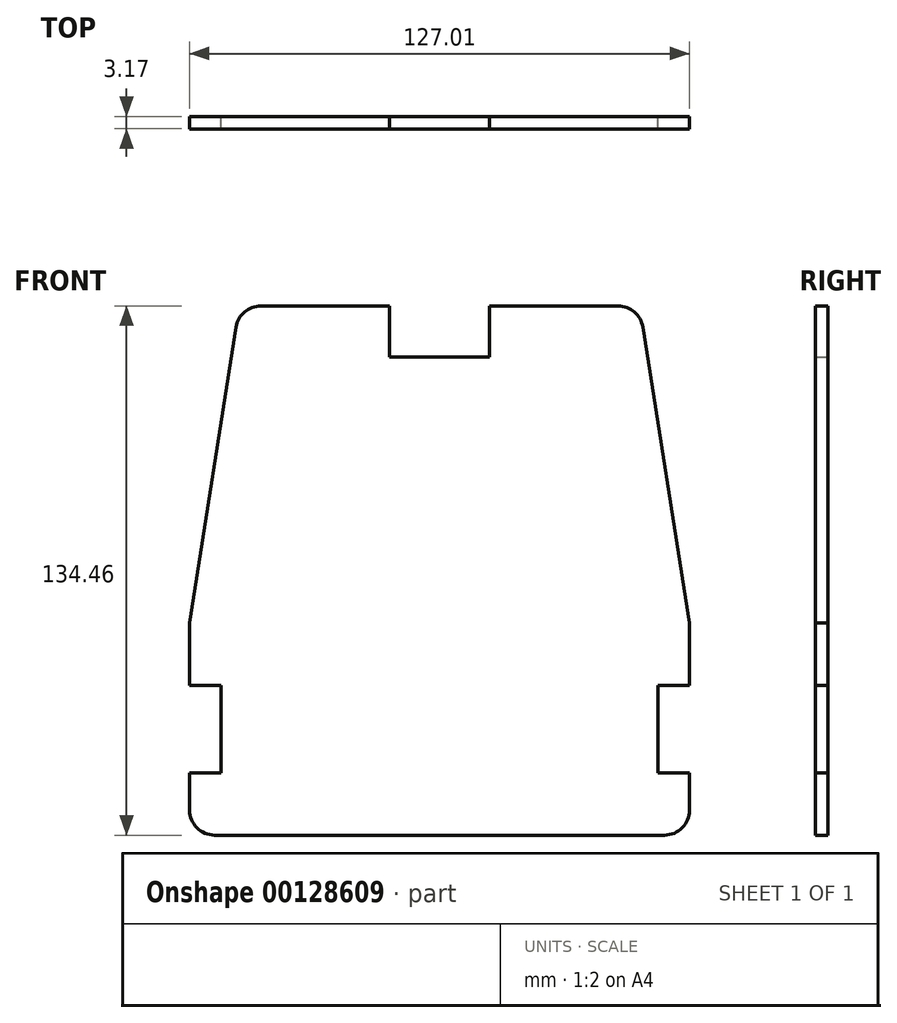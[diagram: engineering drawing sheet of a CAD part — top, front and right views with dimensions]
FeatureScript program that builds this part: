
annotation { "Feature Type Name" : "Feature", "Feature Type Description" : "" }
export const myFeature = defineFeature(function(context is Context, id is Id, definition is map)
    precondition{}
    {
        {
            var Q0;
            Q0=qCreatedBy(makeId("Front.planeOp"),FACE);
            var sketch = newSketch(context, id + "F0", { "sketchPlane" : qUnion([Q0])});
            skLineSegment(sketch, "E0.bottom", {"start": v(-50.8, -3.65) * mm, "end": v(76.2, -3.65) * mm});
            skLineSegment(sketch, "E0.top", {"start": v(-44.44, -57.63) * mm, "end": v(69.86, -57.63) * mm});
            skLineSegment(sketch, "E1", {"start": v(-38.95, 71.47) * mm, "end": v(-50.8, -3.65) * mm});
            skLineSegment(sketch, "E2", {"start": v(64.35, 71.47) * mm, "end": v(76.2, -3.65) * mm});
            skLineSegment(sketch, "E3", {"start": v(-32.67, 76.83) * mm, "end": v(0, 76.83) * mm});
            skLineSegment(sketch, "E4", {"start": v(58.07, 76.83) * mm, "end": v(25.4, 76.83) * mm});
            skLineSegment(sketch, "E5", {"start": v(-50.79, -41.75) * mm, "end": v(-42.85, -41.75) * mm});
            skLineSegment(sketch, "E6", {"start": v(-50.8, -19.53) * mm, "end": v(-42.85, -19.53) * mm});
            skLineSegment(sketch, "E7", {"start": v(-42.85, -19.53) * mm, "end": v(-42.85, -41.75) * mm});
            skLineSegment(sketch, "E8", {"start": v(-50.8, -19.53) * mm, "end": v(-50.8, -3.65) * mm});
            skLineSegment(sketch, "E9", {"start": v(-50.79, -41.75) * mm, "end": v(-50.79, -51.28) * mm});
            skLineSegment(sketch, "E10", {"start": v(76.2, -3.65) * mm, "end": v(76.2, -19.53) * mm});
            skLineSegment(sketch, "E11", {"start": v(76.21, -51.28) * mm, "end": v(76.21, -41.75) * mm});
            skLineSegment(sketch, "E12", {"start": v(76.2, -19.53) * mm, "end": v(68.25, -19.53) * mm});
            skLineSegment(sketch, "E13", {"start": v(68.25, -19.53) * mm, "end": v(68.25, -41.75) * mm});
            skLineSegment(sketch, "E14", {"start": v(68.25, -41.75) * mm, "end": v(76.21, -41.75) * mm});
            skLineSegment(sketch, "E15", {"start": v(0, 76.83) * mm, "end": v(0, 63.9) * mm});
            skLineSegment(sketch, "E16", {"start": v(25.4, 76.83) * mm, "end": v(25.4, 63.9) * mm});
            skLineSegment(sketch, "E17", {"start": v(0, 63.9) * mm, "end": v(25.4, 63.9) * mm});
            skPoint(sketch, "E18.visualSharp", {"position": v(-38.1, 76.83) * mm});
            skArc(sketch, "E18.filletArc", {"start": v(-32.67, 76.83) * mm, "mid": v(-36.8, 75.3) * mm, "end": v(-38.95, 71.47) * mm});
            skPoint(sketch, "E19.visualSharp", {"position": v(63.5, 76.83) * mm});
            skArc(sketch, "E19.filletArc", {"start": v(64.35, 71.47) * mm, "mid": v(62.2, 75.3) * mm, "end": v(58.07, 76.83) * mm});
            skPoint(sketch, "E20.visualSharp", {"position": v(76.21, -57.63) * mm});
            skArc(sketch, "E20.filletArc", {"start": v(69.86, -57.63) * mm, "mid": v(74.35, -55.77) * mm, "end": v(76.21, -51.28) * mm});
            skPoint(sketch, "E21.visualSharp", {"position": v(-50.79, -57.63) * mm});
            skArc(sketch, "E21.filletArc", {"start": v(-50.79, -51.28) * mm, "mid": v(-48.93, -55.77) * mm, "end": v(-44.44, -57.63) * mm});
            skSolve(sketch);
        }
        {
            var Q0;
            Q0 = qSketchRegion(id + "F0", true);
            extrude(context, id + "F1", {"entities" : qUnion([Q0]), "depth" : 3.17 * mm});
        }
    });
